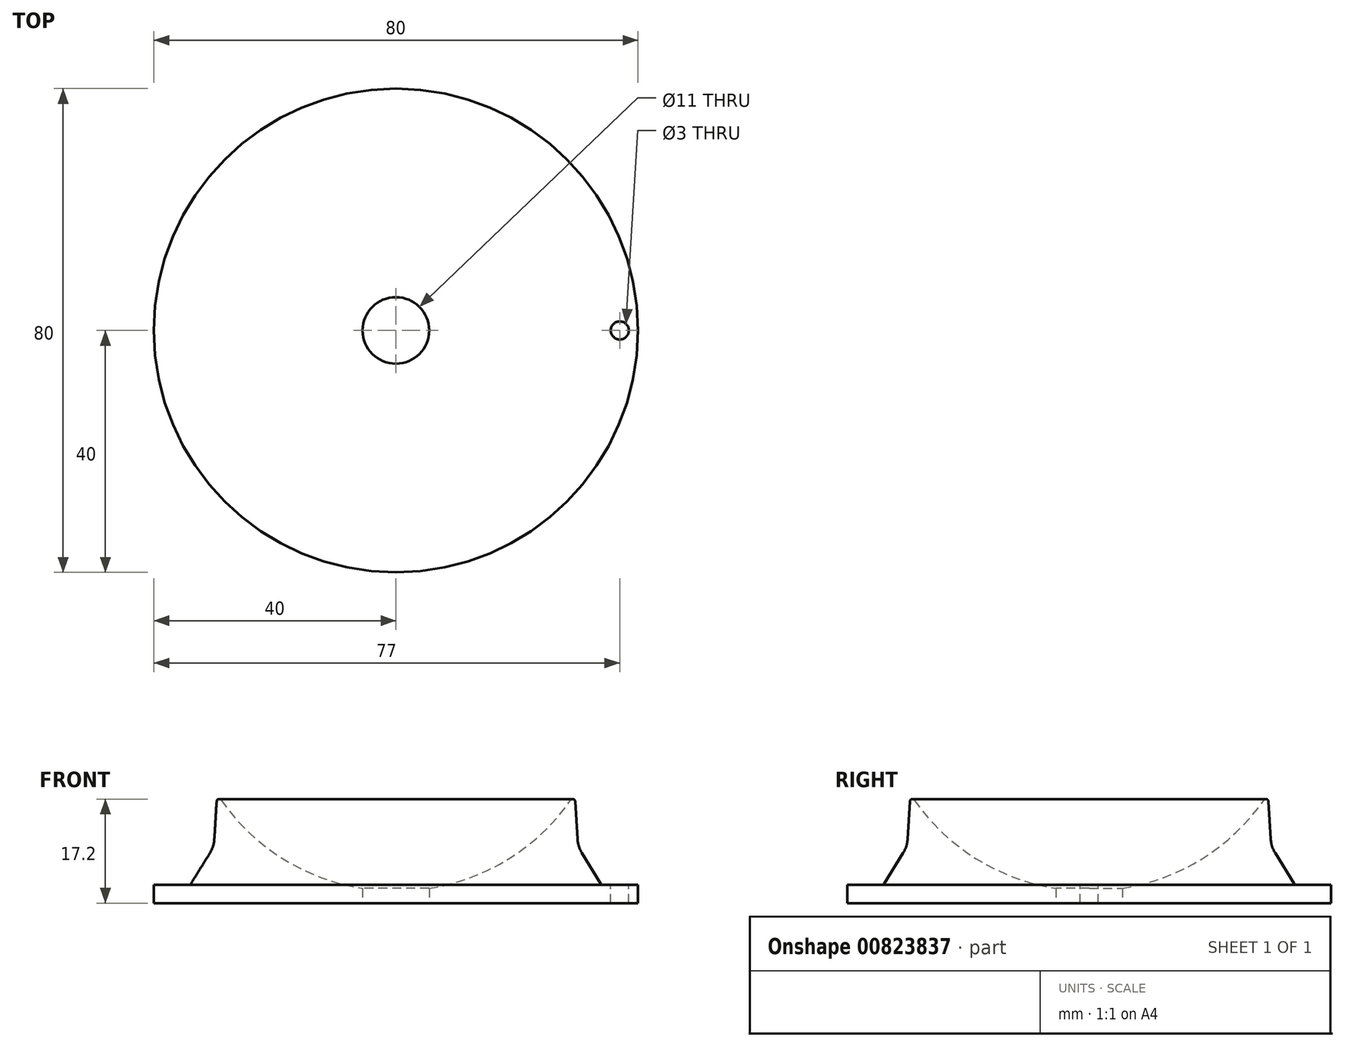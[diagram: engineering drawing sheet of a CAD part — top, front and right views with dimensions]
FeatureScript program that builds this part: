
annotation { "Feature Type Name" : "Feature", "Feature Type Description" : "" }
export const myFeature = defineFeature(function(context is Context, id is Id, definition is map)
    precondition{}
    {
        {
            var Q0;
            Q0=qCreatedBy(makeId("Front.planeOp"),FACE);
            var sketch = newSketch(context, id + "F0", { "sketchPlane" : qUnion([Q0])});
            skLineSegment(sketch, "E0", {"start": v(0, 0) * mm, "end": v(40, 0) * mm});
            skLineSegment(sketch, "E1", {"start": v(40, 0) * mm, "end": v(40, 3) * mm});
            skLineSegment(sketch, "E2", {"start": v(40, 3) * mm, "end": v(34, 3) * mm});
            skLineSegment(sketch, "E3", {"start": v(34, 3) * mm, "end": v(30.09, 9.34) * mm});
            skLineSegment(sketch, "E4", {"start": v(30.09, 9.34) * mm, "end": v(29.56, 18) * mm});
            skArc(sketch, "E5", {"start": v(29.56, 18) * mm, "mid": v(16.8, 6.26) * mm, "end": v(0, 2) * mm});
            skLineSegment(sketch, "E6", {"start": v(0, 2) * mm, "end": v(0, 0) * mm});
            skSolve(sketch);
        }
        {
            var Q0;
            Q0=makeQuery(id+"F0.imprint","IMPRINT",FACE,{"disambiguationData":[TD([[makeQuery(id+"F0.imprint","IMPRINT",EDGE,{"derivedFrom":sQuery(id+"F0.wireOp",EDGE,"E0")}),1.0]])]});
            var Q1;
            Q1=sQuery(id+"F0.wireOp",EDGE,"E6");
            revolve(context, id + "F1", {"surfaceOperationType" : NewSurfaceOperationType.NEW, "entities" : qUnion([Q0]), "axis" : qUnion([Q1]), "revolveType" : RevolveType.FULL});
        }
        {
            var Q0;
            Q0=makeQuery(id+"F1.opRevolve","SWEPT_EDGE",EDGE,{"disambiguationData":[OSD([sQuery(id+"F0.wireOp",EDGE,"E4"),sQuery(id+"F0.wireOp",EDGE,"E5")])]});
            fillet(context, id + "F2", {"entities" : qUnion([Q0]), "radius" : .40 * mm, "tangentPropagation" : true, "allowEdgeOverflow" : false});
        }
        {
            var Q0;
            Q0=makeQuery(id+"F1.opRevolve","SWEPT_EDGE",EDGE,{"disambiguationData":[OSD([sQuery(id+"F0.wireOp",EDGE,"E3"),sQuery(id+"F0.wireOp",EDGE,"E4")])]});
            fillet(context, id + "F3", {"entities" : qUnion([Q0]), "radius" : 5 * mm, "tangentPropagation" : true, "allowEdgeOverflow" : false});
        }
        {
            var Q0;
            Q0=makeQuery(id+"F1.opRevolve","SWEPT_EDGE",EDGE,{"disambiguationData":[OSD([sQuery(id+"F0.wireOp",EDGE,"E2"),sQuery(id+"F0.wireOp",EDGE,"E3")])]});
            fillet(context, id + "F4", {"entities" : qUnion([Q0]), "radius" : .5 * mm, "tangentPropagation" : true, "allowEdgeOverflow" : false});
        }
        {
            var Q0;
            Q0=makeQuery(id+"F1.opRevolve","SWEPT_FACE",FACE,{"disambiguationData":[OSD([sQuery(id+"F0.wireOp",EDGE,"E0")])]});
            var sketch = newSketch(context, id + "F5", { "sketchPlane" : qUnion([Q0])});
            skPoint(sketch, "E7", {"position": v(0, 0) * mm});
            skCircle(sketch, "E8", {"center": v(0, 0) * mm, "radius": 5.5 * mm});
            skSolve(sketch);
        }
        {
            var Q0;
            Q0 = qSketchRegion(id + "F5", true);
            extrude(context, id + "F6", {"entities" : qUnion([Q0]), "operationType" : NewBodyOperationType.REMOVE, "endBound" : BoundingType.UP_TO_NEXT, "oppositeDirection" : true, "depth" : 25 * mm, "offsetDistance" : 25 * mm});
        }
        {
            var Q0;
            Q0=makeQuery(id+"F1.opRevolve","SWEPT_FACE",FACE,{"disambiguationData":[OSD([sQuery(id+"F0.wireOp",EDGE,"E2")])]});
            var sketch = newSketch(context, id + "F7", { "sketchPlane" : qUnion([Q0])});
            skCircle(sketch, "E9", {"center": v(0, 0) * mm, "radius": 37 * mm, "construction": true});
            skCircle(sketch, "E10", {"center": v(37, 0) * mm, "radius": 1.5 * mm});
            skSolve(sketch);
        }
        {
            var Q0;
            Q0=makeQuery(id+"F7.imprint","IMPRINT",FACE,{"disambiguationData":[TD([[makeQuery(id+"F7.imprint","IMPRINT",EDGE,{"derivedFrom":sQuery(id+"F7.wireOp",EDGE,"E10")}),1.0]])]});
            extrude(context, id + "F8", {"entities" : qUnion([Q0]), "operationType" : NewBodyOperationType.REMOVE, "endBound" : BoundingType.UP_TO_NEXT, "oppositeDirection" : true, "depth" : 25 * mm, "offsetDistance" : 25 * mm});
        }
    });
